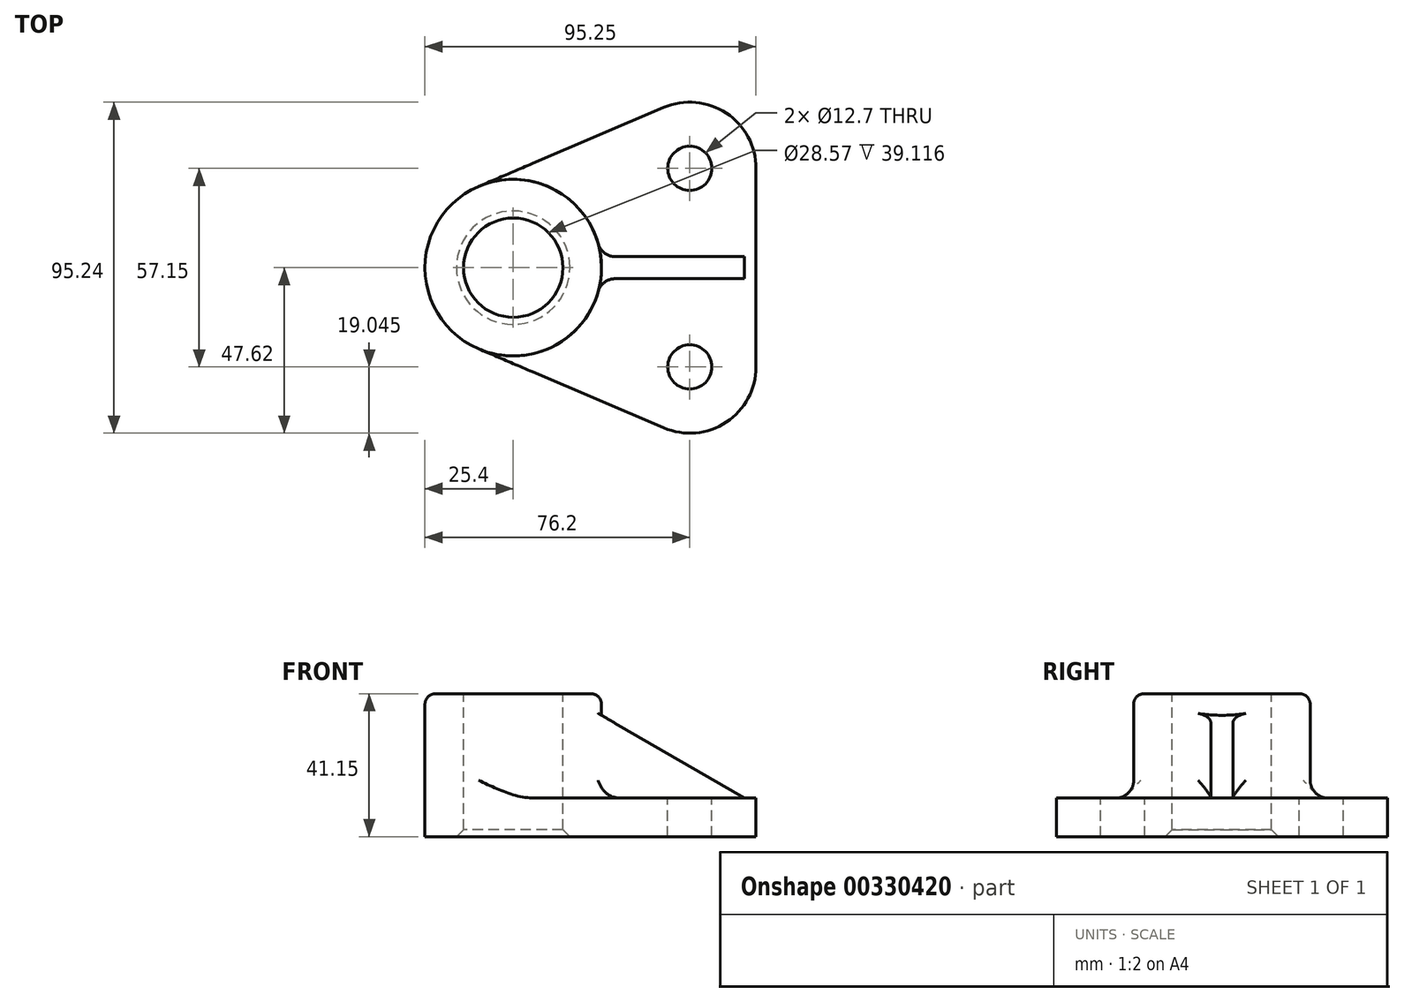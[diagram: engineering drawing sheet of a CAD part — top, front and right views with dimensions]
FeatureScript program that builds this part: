
annotation { "Feature Type Name" : "Feature", "Feature Type Description" : "" }
export const myFeature = defineFeature(function(context is Context, id is Id, definition is map)
    precondition{}
    {
        {
            var Q0;
            Q0=qCreatedBy(makeId("Top.planeOp"),FACE);
            var sketch = newSketch(context, id + "F0", { "sketchPlane" : qUnion([Q0])});
            skCircle(sketch, "E0", {"center": v(0, 0) * mm, "radius": 25.4 * mm});
            skLineSegment(sketch, "E1", {"start": v(-9.97, 23.36) * mm, "end": v(43.33, 46.1) * mm});
            skLineSegment(sketch, "E2", {"start": v(69.85, 28.58) * mm, "end": v(69.85, -28.57) * mm});
            skLineSegment(sketch, "E3", {"start": v(43.33, -46.1) * mm, "end": v(-9.97, -23.36) * mm});
            skPoint(sketch, "E4.visualSharp", {"position": v(69.85, 57.41) * mm});
            skArc(sketch, "E4.filletArc", {"start": v(69.85, 28.58) * mm, "mid": v(61.3, 44.47) * mm, "end": v(43.33, 46.1) * mm});
            skPoint(sketch, "E5.visualSharp", {"position": v(69.85, -57.41) * mm});
            skArc(sketch, "E5.filletArc", {"start": v(43.33, -46.1) * mm, "mid": v(61.3, -44.47) * mm, "end": v(69.85, -28.57) * mm});
            skSolve(sketch);
        }
        {
            var Q0;
            {var subQ0=sQuery(id+"F0.wireOp",EDGE,"E0");var subQ1=makeQuery(id+"F0.imprint","INTERSECT",VERTEX,{"derivedFrom":[subQ0,sQuery(id+"F0.wireOp",EDGE,"E1")]});Q0=makeQuery(id+"F0.imprint","IMPRINT",FACE,{"disambiguationData":[TD([[makeQuery(id+"F0.imprint","IMPRINT",EDGE,{"disambiguationData":[TD([[subQ1,-1.0]])],"derivedFrom":subQ0}),1.0]])]});}
            var Q1;
            {var subQ1=sQuery(id+"F0.wireOp",EDGE,"E1");Q1=makeQuery(id+"F0.imprint","IMPRINT",FACE,{"disambiguationData":[TD([[makeQuery(id+"F0.imprint","IMPRINT",EDGE,{"derivedFrom":subQ1}),-1.0]])]});}
            extrude(context, id + "F1", {"entities" : qUnion([Q0, Q1]), "depth" : 11.18 * mm});
        }
        {
            var Q0;
            Q0=qCreatedBy(makeId("Top.planeOp"),FACE);
            var sketch = newSketch(context, id + "F2", { "sketchPlane" : qUnion([Q0])});
            skCircle(sketch, "E6", {"center": v(0, 0) * mm, "radius": 25.4 * mm});
            skSolve(sketch);
        }
        {
            var Q0;
            Q0 = qSketchRegion(id + "F2", true);
            extrude(context, id + "F3", {"entities" : qUnion([Q0]), "operationType" : NewBodyOperationType.ADD, "depth" : 41.15 * mm});
        }
        {
            var Q0;
            Q0=makeQuery(id+"F3.opExtrude","CAP_EDGE",EDGE,{"disambiguationData":[OSD([sQuery(id+"F2.wireOp",EDGE,"E6")])],"isStart":false});
            fillet(context, id + "F4", {"entities" : qUnion([Q0]), "radius" : 3.05 * mm, "tangentPropagation" : true, "allowEdgeOverflow" : false});
        }
        {
            var Q0;
            Q0=qCreatedBy(makeId("Front.planeOp"),FACE);
            var sketch = newSketch(context, id + "F5", { "sketchPlane" : qUnion([Q0])});
            skLineSegment(sketch, "E7", {"start": v(17.04, 39.76) * mm, "end": v(66.55, 11.18) * mm});
            skLineSegment(sketch, "E8", {"start": v(66.55, 11.18) * mm, "end": v(17.04, 11.18) * mm});
            skLineSegment(sketch, "E9", {"start": v(17.04, 11.18) * mm, "end": v(17.04, 39.76) * mm});
            skSolve(sketch);
        }
        {
            var Q0;
            Q0=makeQuery(id+"F5.imprint","IMPRINT",FACE,{"disambiguationData":[TD([[makeQuery(id+"F5.imprint","IMPRINT",EDGE,{"derivedFrom":sQuery(id+"F5.wireOp",EDGE,"E7")}),-1.0]])]});
            extrude(context, id + "F6", {"entities" : qUnion([Q0]), "operationType" : NewBodyOperationType.ADD, "endBound" : BoundingType.SYMMETRIC, "depth" : 6.35 * mm});
        }
        {
            var Q0;
            Q0=makeQuery(id+"F3.opExtrude","CAP_FACE",FACE,{"disambiguationData":[OSD([sQuery(id+"F2.wireOp",EDGE,"E6")])],"isStart":false});
            var sketch = newSketch(context, id + "F7", { "sketchPlane" : qUnion([Q0])});
            skCircle(sketch, "E10", {"center": v(0, 0) * mm, "radius": 14.29 * mm});
            skCircle(sketch, "E11", {"center": v(50.8, 28.58) * mm, "radius": 6.35 * mm});
            skCircle(sketch, "E12", {"center": v(50.8, -28.57) * mm, "radius": 6.35 * mm});
            skSolve(sketch);
        }
        {
            var Q0;
            Q0=makeQuery(id+"F7.imprint","IMPRINT",FACE,{"disambiguationData":[TD([[makeQuery(id+"F7.imprint","IMPRINT",EDGE,{"derivedFrom":sQuery(id+"F7.wireOp",EDGE,"E10")}),1.0]])]});
            var Q1;
            Q1=makeQuery(id+"F7.imprint","IMPRINT",FACE,{"disambiguationData":[TD([[makeQuery(id+"F7.imprint","IMPRINT",EDGE,{"derivedFrom":sQuery(id+"F7.wireOp",EDGE,"E11")}),1.0]])]});
            var Q2;
            Q2=makeQuery(id+"F7.imprint","IMPRINT",FACE,{"disambiguationData":[TD([[makeQuery(id+"F7.imprint","IMPRINT",EDGE,{"derivedFrom":sQuery(id+"F7.wireOp",EDGE,"E12")}),1.0]])]});
            extrude(context, id + "F8", {"entities" : qUnion([Q0, Q1, Q2]), "operationType" : NewBodyOperationType.REMOVE, "endBound" : BoundingType.THROUGH_ALL, "oppositeDirection" : true, "depth" : 25.4 * mm});
        }
        {
            var Q0;
            Q0=makeQuery(id+"F8.boolean.opBoolean","COPY",EDGE,{"derivedFrom":makeQuery(id+"F8.opExtrude","CAP_EDGE",EDGE,{"disambiguationData":[OSD([sQuery(id+"F7.wireOp",EDGE,"E10")])],"isStart":true})});
            var Q1;
            Q1=makeQuery(id+"F8.boolean.opBoolean","INTERSECT",EDGE,{"derivedFrom":[makeQuery(id+"F1.opExtrude","CAP_FACE",FACE,{"disambiguationData":[OSD([sQuery(id+"F0.wireOp",EDGE,"E0"),sQuery(id+"F0.wireOp",EDGE,"E1"),sQuery(id+"F0.wireOp",EDGE,"E2"),sQuery(id+"F0.wireOp",EDGE,"E3"),sQuery(id+"F0.wireOp",EDGE,"E4.filletArc"),sQuery(id+"F0.wireOp",EDGE,"E5.filletArc")])],"isStart":true}),makeQuery(id+"F8.opExtrude","SWEPT_FACE",FACE,{"disambiguationData":[OSD([sQuery(id+"F7.wireOp",EDGE,"E10")])]})]});
            chamfer(context, id + "F9", {"entities" : qUnion([Q0, Q1]), "width" : 2.03 * mm, "tangentPropagation" : true});
        }
        {
            var Q0;
            {var subQ0=makeQuery(id+"F3.opExtrude","SWEPT_FACE",FACE,{"disambiguationData":[OSD([sQuery(id+"F2.wireOp",EDGE,"E6")])]});var subQ1=sQuery(id+"F0.wireOp",EDGE,"E3");var subQ2=sQuery(id+"F0.wireOp",EDGE,"E0");var subQ3=makeQuery(id+"F1.opExtrude","CAP_FACE",FACE,{"disambiguationData":[OSD([subQ2,sQuery(id+"F0.wireOp",EDGE,"E1"),sQuery(id+"F0.wireOp",EDGE,"E2"),subQ1,sQuery(id+"F0.wireOp",EDGE,"E4.filletArc"),sQuery(id+"F0.wireOp",EDGE,"E5.filletArc")])],"isStart":false});Q0=makeQuery(id+"F6.boolean.opBoolean","SPLIT",EDGE,{"disambiguationData":[TD([makeQuery(id+"F1.opExtrude","SWEPT_FACE",FACE,{"disambiguationData":[OSD([subQ1])]})])],"derivedFrom":makeQuery(id+"F3.boolean.opBoolean","INTERSECT",EDGE,{"derivedFrom":[subQ3,subQ0]})});}
            var Q1;
            {var subQ0=makeQuery(id+"F3.opExtrude","SWEPT_FACE",FACE,{"disambiguationData":[OSD([sQuery(id+"F2.wireOp",EDGE,"E6")])]});var subQ1=sQuery(id+"F0.wireOp",EDGE,"E1");var subQ2=sQuery(id+"F0.wireOp",EDGE,"E0");var subQ3=makeQuery(id+"F1.opExtrude","CAP_FACE",FACE,{"disambiguationData":[OSD([subQ2,subQ1,sQuery(id+"F0.wireOp",EDGE,"E2"),sQuery(id+"F0.wireOp",EDGE,"E3"),sQuery(id+"F0.wireOp",EDGE,"E4.filletArc"),sQuery(id+"F0.wireOp",EDGE,"E5.filletArc")])],"isStart":false});Q1=makeQuery(id+"F6.boolean.opBoolean","SPLIT",EDGE,{"disambiguationData":[TD([makeQuery(id+"F1.opExtrude","SWEPT_FACE",FACE,{"disambiguationData":[OSD([subQ1])]})])],"derivedFrom":makeQuery(id+"F3.boolean.opBoolean","INTERSECT",EDGE,{"derivedFrom":[subQ3,subQ0]})});}
            var Q2;
            Q2=makeQuery(id+"F6.boolean.opBoolean","INTERSECT",EDGE,{"derivedFrom":[makeQuery(id+"F3.boolean.opBoolean","MERGE",FACE,{"derivedFrom":[makeQuery(id+"F1.opExtrude","SWEPT_FACE",FACE,{"disambiguationData":[OSD([sQuery(id+"F0.wireOp",EDGE,"E0")])]}),makeQuery(id+"F3.opExtrude","SWEPT_FACE",FACE,{"disambiguationData":[OSD([sQuery(id+"F2.wireOp",EDGE,"E6")])]})]}),makeQuery(id+"F6.opExtrude","CAP_FACE",FACE,{"disambiguationData":[OSD([sQuery(id+"F5.wireOp",EDGE,"E7"),sQuery(id+"F5.wireOp",EDGE,"E8"),sQuery(id+"F5.wireOp",EDGE,"E9")])],"isStart":true})]});
            var Q3;
            Q3=makeQuery(id+"F6.opExtrude","CAP_EDGE",EDGE,{"disambiguationData":[OSD([sQuery(id+"F5.wireOp",EDGE,"E8")])],"isStart":true});
            var Q4;
            Q4=makeQuery(id+"F6.opExtrude","CAP_EDGE",EDGE,{"disambiguationData":[OSD([sQuery(id+"F5.wireOp",EDGE,"E8")])],"isStart":false});
            var Q5;
            Q5=makeQuery(id+"F6.boolean.opBoolean","INTERSECT",EDGE,{"derivedFrom":[makeQuery(id+"F3.boolean.opBoolean","MERGE",FACE,{"derivedFrom":[makeQuery(id+"F1.opExtrude","SWEPT_FACE",FACE,{"disambiguationData":[OSD([sQuery(id+"F0.wireOp",EDGE,"E0")])]}),makeQuery(id+"F3.opExtrude","SWEPT_FACE",FACE,{"disambiguationData":[OSD([sQuery(id+"F2.wireOp",EDGE,"E6")])]})]}),makeQuery(id+"F6.opExtrude","CAP_FACE",FACE,{"disambiguationData":[OSD([sQuery(id+"F5.wireOp",EDGE,"E7"),sQuery(id+"F5.wireOp",EDGE,"E8"),sQuery(id+"F5.wireOp",EDGE,"E9")])],"isStart":false})]});
            fillet(context, id + "F10", {"entities" : qUnion([Q0, Q1, Q2, Q3, Q4, Q5]), "radius" : 5.08 * mm, "tangentPropagation" : true, "allowEdgeOverflow" : false});
        }
    });
